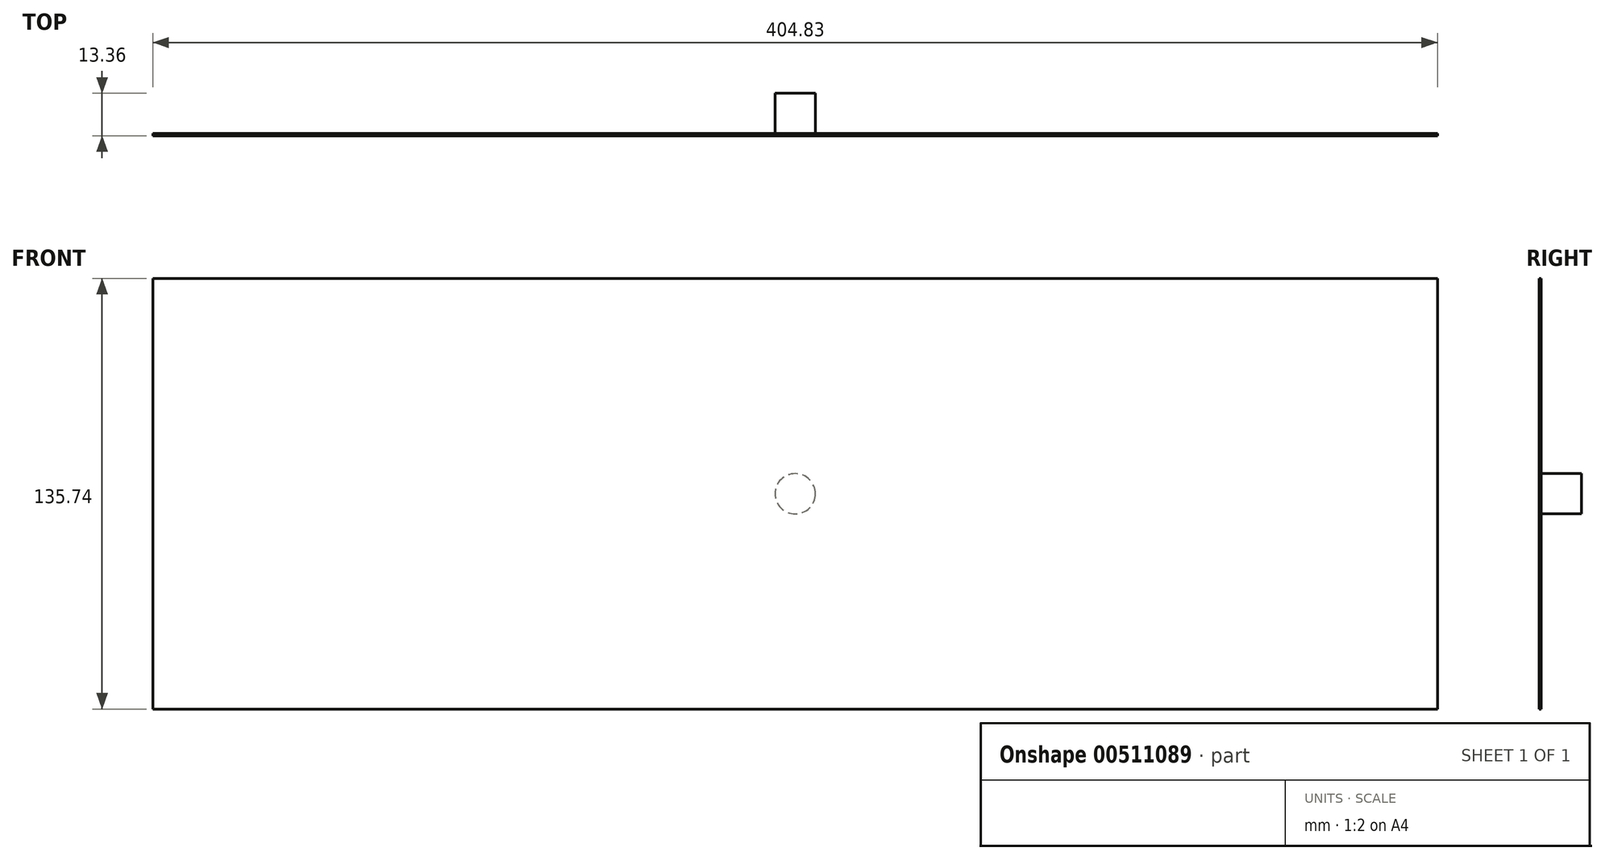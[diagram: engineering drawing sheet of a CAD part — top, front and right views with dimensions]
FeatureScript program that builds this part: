
annotation { "Feature Type Name" : "Feature", "Feature Type Description" : "" }
export const myFeature = defineFeature(function(context is Context, id is Id, definition is map)
    precondition{}
    {
        {
            assignVariable(context, id + "F0", {"name" : "thickness", "anyValue" : 0.66});
        }
        {
            var Q0;
            Q0=qCreatedBy(makeId("Front.planeOp"),FACE);
            var sketch = newSketch(context, id + "F1", { "sketchPlane" : qUnion([Q0])});
            skLineSegment(sketch, "E0.bottom", {"start": v(-404.83, 135.74) * mm, "end": v(0, 135.74) * mm});
            skLineSegment(sketch, "E0.top", {"start": v(-404.83, 0) * mm, "end": v(0, 0) * mm});
            skLineSegment(sketch, "E0.left", {"start": v(-404.83, 135.74) * mm, "end": v(-404.83, 0) * mm});
            skLineSegment(sketch, "E0.right", {"start": v(0, 135.74) * mm, "end": v(0, 0) * mm});
            skSolve(sketch);
        }
        {
            var Q0;
            Q0=makeQuery(id+"F1.imprint","IMPRINT",FACE,{"disambiguationData":[TD([[makeQuery(id+"F1.imprint","IMPRINT",EDGE,{"derivedFrom":sQuery(id+"F1.wireOp",EDGE,"E0.bottom")}),-1.0]])]});
            extrude(context, id + "F2", {"entities" : qUnion([Q0]), "depth" : (getVariable(context, 'thickness')) * mm, "offsetDistance" : 25.4 * mm});
        }
        {
            var Q0;
            Q0=makeQuery(id+"F2.opExtrude","CAP_FACE",FACE,{"disambiguationData":[OSD([sQuery(id+"F1.wireOp",EDGE,"E0.bottom"),sQuery(id+"F1.wireOp",EDGE,"E0.top"),sQuery(id+"F1.wireOp",EDGE,"E0.left"),sQuery(id+"F1.wireOp",EDGE,"E0.right")])],"isStart":true});
            var sketch = newSketch(context, id + "F3", { "sketchPlane" : qUnion([Q0])});
            skLineSegment(sketch, "E1.0.0", {"start": v(404.83, 135.74) * mm, "end": v(404.83, 0) * mm, "construction": true});
            skLineSegment(sketch, "E1.0.1", {"start": v(404.83, 0) * mm, "end": v(0, 0) * mm, "construction": true});
            skLineSegment(sketch, "E1.0.2", {"start": v(0, 0) * mm, "end": v(0, 135.74) * mm, "construction": true});
            skLineSegment(sketch, "E1.0.3", {"start": v(0, 135.74) * mm, "end": v(404.83, 135.74) * mm, "construction": true});
            skCircle(sketch, "E2", {"center": v(202.41, 67.87) * mm, "radius": 6.35 * mm});
            skPoint(sketch, "E2.centerSnap0", {"position": v(202.41, 135.74) * mm});
            skPoint(sketch, "E2.centerSnap1", {"position": v(0, 67.87) * mm});
            skSolve(sketch);
        }
        {
            var Q0;
            Q0 = qSketchRegion(id + "F3", true);
            extrude(context, id + "F4", {"entities" : qUnion([Q0]), "operationType" : NewBodyOperationType.ADD, "depth" : 12.7 * mm, "offsetDistance" : 25.4 * mm});
        }
    });
